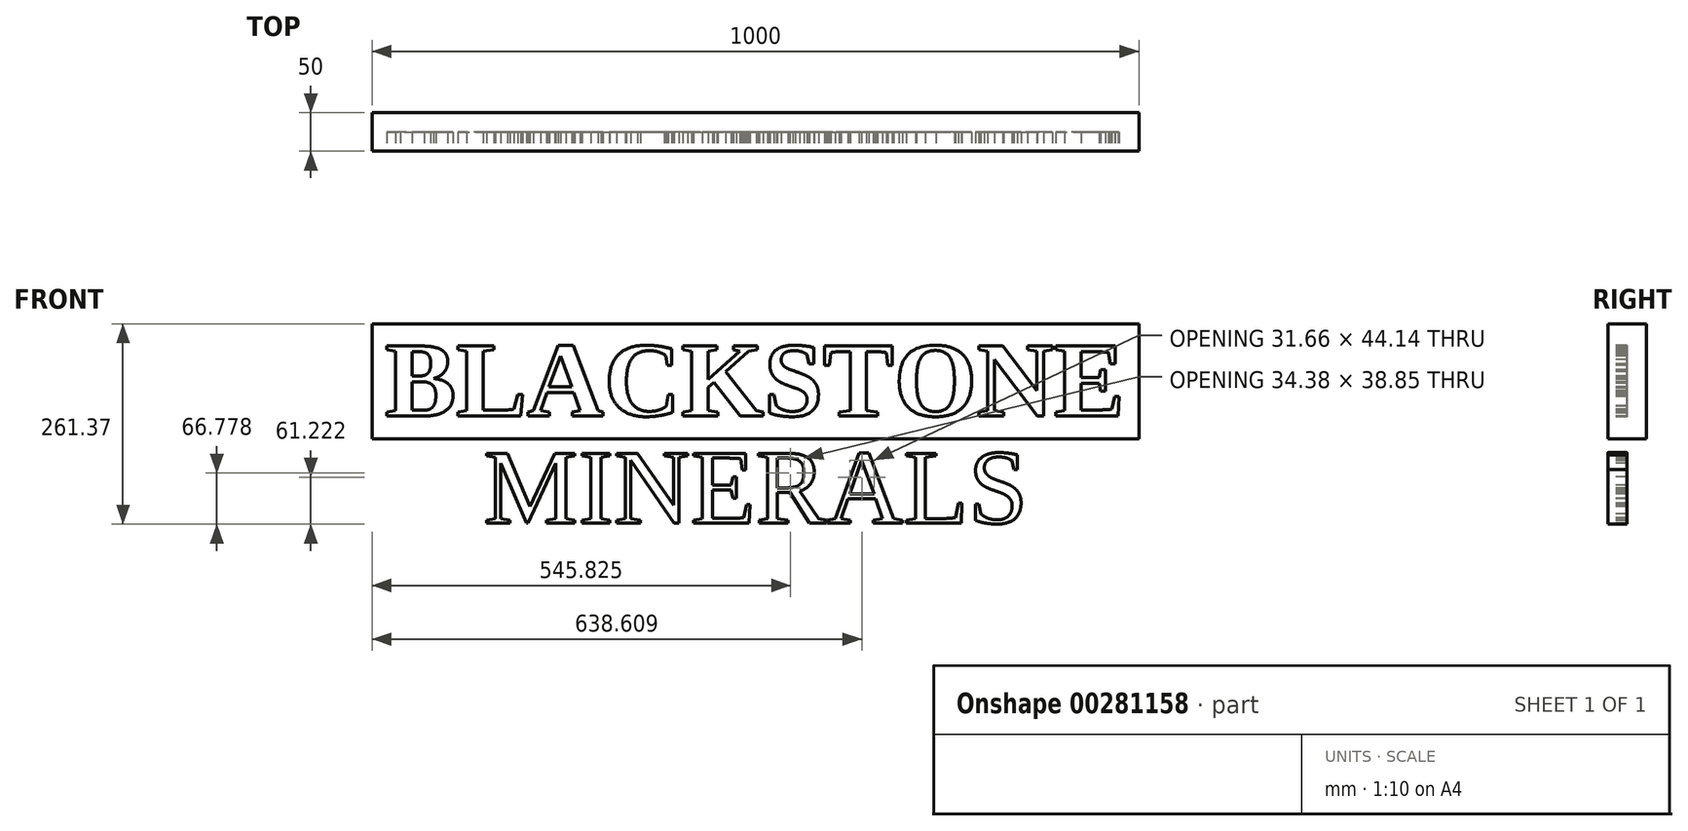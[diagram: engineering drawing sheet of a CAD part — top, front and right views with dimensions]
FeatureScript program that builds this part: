
annotation { "Feature Type Name" : "Feature", "Feature Type Description" : "" }
export const myFeature = defineFeature(function(context is Context, id is Id, definition is map)
    precondition{}
    {
        {
            var Q0;
            Q0=qCreatedBy(makeId("Front.planeOp"),FACE);
            var sketch = newSketch(context, id + "F0", { "sketchPlane" : qUnion([Q0])});
            skLineSegment(sketch, "E0.bottom", {"start": v(500, -10) * mm, "end": v(-500, -10) * mm});
            skLineSegment(sketch, "E0.top", {"start": v(500, 140) * mm, "end": v(-500, 140) * mm});
            skLineSegment(sketch, "E0.left", {"start": v(500, -10) * mm, "end": v(500, 140) * mm});
            skLineSegment(sketch, "E0.right", {"start": v(-500, -10) * mm, "end": v(-500, 140) * mm});
            skSolve(sketch);
        }
        {
            var Q0;
            Q0 = qSketchRegion(id + "F0", true);
            extrude(context, id + "F1", {"entities" : qUnion([Q0]), "oppositeDirection" : true, "depth" : 50 * mm});
        }
        {
            var Q0;
            Q0=qCreatedBy(makeId("Front.planeOp"),FACE);
            var sketch = newSketch(context, id + "F2", { "sketchPlane" : qUnion([Q0])});
            skText(sketch, "E1", { "text": "BLACKSTONE", "fontName": "Tinos-Bold.ttf"});
            const initialGuessF2  = {"E1": [-0.48317, 0.02, 1, 0, 0.1]};
            skSetInitialGuess(sketch, initialGuessF2);
            skSolve(sketch);
        }
        {
            var Q0;
            Q0 = qSketchRegion(id + "F2", true);
            extrude(context, id + "F3", {"entities" : qUnion([Q0]), "operationType" : NewBodyOperationType.REMOVE, "oppositeDirection" : true, "depth" : 25 * mm});
        }
        {
            var Q0;
            Q0=qCreatedBy(makeId("Front.planeOp"),FACE);
            var sketch = newSketch(context, id + "F4", { "sketchPlane" : qUnion([Q0])});
            skText(sketch, "E2", { "text": "MINERALS", "fontName": "Tinos-Regular.ttf"});
            const initialGuessF4  = {"E2": [-0.355, -0.12, 1, 0, 0.1]};
            skSetInitialGuess(sketch, initialGuessF4);
            skSolve(sketch);
        }
        {
            var Q0;
            Q0 = qSketchRegion(id + "F4", true);
            extrude(context, id + "F5", {"entities" : qUnion([Q0]), "oppositeDirection" : true, "depth" : 25 * mm});
        }
    });
